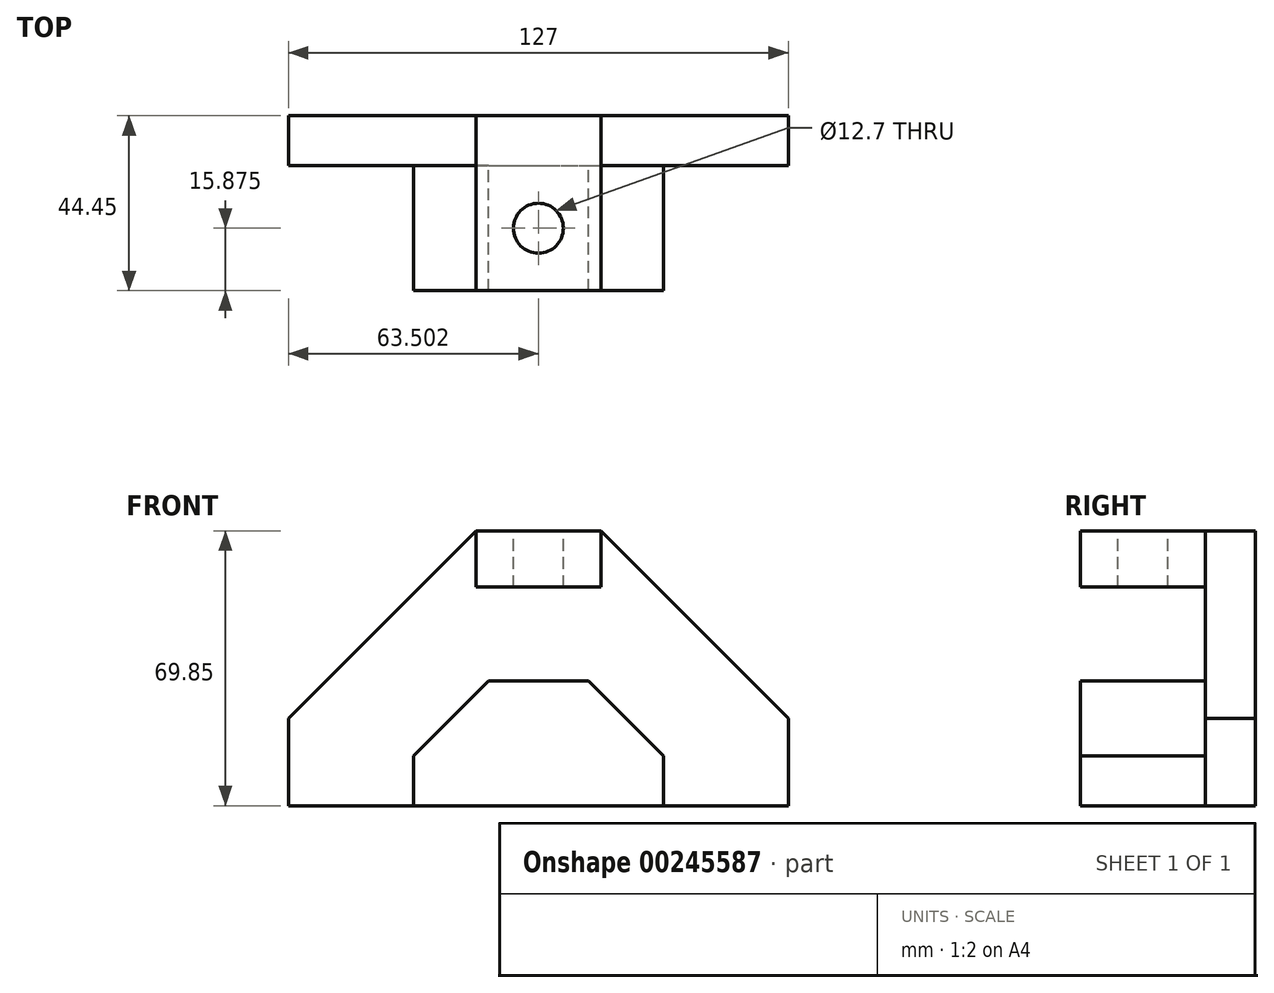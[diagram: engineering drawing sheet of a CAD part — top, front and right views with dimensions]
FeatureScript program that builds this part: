
annotation { "Feature Type Name" : "Feature", "Feature Type Description" : "" }
export const myFeature = defineFeature(function(context is Context, id is Id, definition is map)
    precondition{}
    {
        {
            var Q0;
            Q0=qCreatedBy(makeId("Front.planeOp"),FACE);
            var sketch = newSketch(context, id + "F0", { "sketchPlane" : qUnion([Q0])});
            skLineSegment(sketch, "E0.bottom", {"start": v(-62.96, 52.97) * mm, "end": v(64.04, 52.97) * mm});
            skLineSegment(sketch, "E0.top", {"start": v(-62.96, -16.88) * mm, "end": v(64.04, -16.88) * mm});
            skLineSegment(sketch, "E0.left", {"start": v(-62.96, 52.97) * mm, "end": v(-62.96, -16.88) * mm});
            skLineSegment(sketch, "E0.right", {"start": v(64.04, 52.97) * mm, "end": v(64.04, -16.88) * mm});
            skLineSegment(sketch, "E1", {"start": v(-15.33, 52.97) * mm, "end": v(-62.96, 5.35) * mm});
            skLineSegment(sketch, "E2", {"start": v(16.42, 52.97) * mm, "end": v(64.04, 5.35) * mm});
            skSolve(sketch);
        }
        {
            var Q0;
            {var subQ1=sQuery(id+"F0.wireOp",EDGE,"E0.top");Q0=makeQuery(id+"F0.imprint","IMPRINT",FACE,{"disambiguationData":[TD([[makeQuery(id+"F0.imprint","IMPRINT",EDGE,{"derivedFrom":subQ1}),1.0]])]});}
            extrude(context, id + "F1", {"entities" : qUnion([Q0]), "depth" : 12.7 * mm});
        }
        {
            var Q0;
            Q0=makeQuery(id+"F1.opExtrude","CAP_FACE",FACE,{"disambiguationData":[OSD([sQuery(id+"F0.wireOp",EDGE,"E0.bottom"),sQuery(id+"F0.wireOp",EDGE,"E0.top"),sQuery(id+"F0.wireOp",EDGE,"E0.left"),sQuery(id+"F0.wireOp",EDGE,"E0.right"),sQuery(id+"F0.wireOp",EDGE,"E1"),sQuery(id+"F0.wireOp",EDGE,"E2")])],"isStart":false});
            var sketch = newSketch(context, id + "F2", { "sketchPlane" : qUnion([Q0])});
            skLineSegment(sketch, "E3.right", {"start": v(13.24, 14.87) * mm, "end": v(13.24, -16.88) * mm});
            skLineSegment(sketch, "E4.bottom", {"start": v(13.24, 14.87) * mm, "end": v(32.3, 14.87) * mm});
            skLineSegment(sketch, "E4.top", {"start": v(13.24, -16.88) * mm, "end": v(32.3, -16.88) * mm});
            skLineSegment(sketch, "E4.right", {"start": v(32.3, 14.87) * mm, "end": v(32.3, -16.88) * mm});
            skLineSegment(sketch, "E5", {"start": v(13.24, 14.87) * mm, "end": v(32.3, -4.18) * mm});
            skSolve(sketch);
        }
        {
            var Q0;
            Q0=makeQuery(id+"F1.opExtrude","CAP_FACE",FACE,{"disambiguationData":[OSD([sQuery(id+"F0.wireOp",EDGE,"E0.bottom"),sQuery(id+"F0.wireOp",EDGE,"E0.top"),sQuery(id+"F0.wireOp",EDGE,"E0.left"),sQuery(id+"F0.wireOp",EDGE,"E0.right"),sQuery(id+"F0.wireOp",EDGE,"E1"),sQuery(id+"F0.wireOp",EDGE,"E2")])],"isStart":false});
            var sketch = newSketch(context, id + "F3", { "sketchPlane" : qUnion([Q0])});
            skLineSegment(sketch, "E6.bottom", {"start": v(-12.16, 14.87) * mm, "end": v(13.24, 14.87) * mm});
            skLineSegment(sketch, "E6.top", {"start": v(-12.16, -16.88) * mm, "end": v(13.24, -16.88) * mm});
            skLineSegment(sketch, "E6.left", {"start": v(-12.16, 14.87) * mm, "end": v(-12.16, -16.88) * mm});
            skLineSegment(sketch, "E6.right", {"start": v(13.24, 14.87) * mm, "end": v(13.24, -16.88) * mm});
            skSolve(sketch);
        }
        {
            var Q0;
            Q0=makeQuery(id+"F3.imprint","IMPRINT",FACE,{"disambiguationData":[TD([[makeQuery(id+"F3.imprint","IMPRINT",EDGE,{"derivedFrom":sQuery(id+"F3.wireOp",EDGE,"E6.bottom")}),1.0]])]});
            var sketch = newSketch(context, id + "F4", { "sketchPlane" : qUnion([Q0])});
            skLineSegment(sketch, "E7.bottom", {"start": v(-31.2, -16.88) * mm, "end": v(-12.16, -16.88) * mm});
            skLineSegment(sketch, "E7.top", {"start": v(-31.2, 14.87) * mm, "end": v(-12.16, 14.87) * mm});
            skLineSegment(sketch, "E7.left", {"start": v(-31.2, -16.88) * mm, "end": v(-31.2, 14.87) * mm});
            skLineSegment(sketch, "E7.right", {"start": v(-12.16, -16.88) * mm, "end": v(-12.16, 14.87) * mm});
            skLineSegment(sketch, "E8", {"start": v(-12.16, 14.87) * mm, "end": v(-31.2, -4.18) * mm});
            skSolve(sketch);
        }
        {
            var Q0;
            {var subQ0=sQuery(id+"F4.wireOp",EDGE,"E7.bottom");Q0=makeQuery(id+"F4.imprint","IMPRINT",FACE,{"disambiguationData":[TD([[makeQuery(id+"F4.imprint","IMPRINT",EDGE,{"derivedFrom":subQ0}),1.0]])]});}
            var Q1;
            {var subQ0=sQuery(id+"F2.wireOp",EDGE,"E4.top");Q1=makeQuery(id+"F2.imprint","IMPRINT",FACE,{"disambiguationData":[TD([[makeQuery(id+"F2.imprint","IMPRINT",EDGE,{"derivedFrom":subQ0}),1.0]])]});}
            var Q2;
            Q2=makeQuery(id+"F3.imprint","IMPRINT",FACE,{"disambiguationData":[TD([[makeQuery(id+"F3.imprint","IMPRINT",EDGE,{"derivedFrom":sQuery(id+"F3.wireOp",EDGE,"E6.bottom")}),-1.0]])]});
            extrude(context, id + "F5", {"entities" : qUnion([Q0, Q1, Q2]), "operationType" : NewBodyOperationType.ADD, "depth" : 31.75 * mm});
        }
        {
            var Q0;
            Q0=makeQuery(id+"F1.opExtrude","CAP_FACE",FACE,{"disambiguationData":[OSD([sQuery(id+"F0.wireOp",EDGE,"E0.bottom"),sQuery(id+"F0.wireOp",EDGE,"E0.top"),sQuery(id+"F0.wireOp",EDGE,"E0.left"),sQuery(id+"F0.wireOp",EDGE,"E0.right"),sQuery(id+"F0.wireOp",EDGE,"E1"),sQuery(id+"F0.wireOp",EDGE,"E2")])],"isStart":false});
            var sketch = newSketch(context, id + "F6", { "sketchPlane" : qUnion([Q0])});
            skLineSegment(sketch, "E9.bottom", {"start": v(-15.33, 52.97) * mm, "end": v(16.42, 52.97) * mm});
            skLineSegment(sketch, "E9.top", {"start": v(-15.33, 38.69) * mm, "end": v(16.42, 38.69) * mm});
            skLineSegment(sketch, "E9.left", {"start": v(-15.33, 52.97) * mm, "end": v(-15.33, 38.69) * mm});
            skLineSegment(sketch, "E9.right", {"start": v(16.42, 52.97) * mm, "end": v(16.42, 38.69) * mm});
            skSolve(sketch);
        }
        {
            var Q0;
            Q0=makeQuery(id+"F6.imprint","IMPRINT",FACE,{"disambiguationData":[TD([[makeQuery(id+"F6.imprint","IMPRINT",EDGE,{"derivedFrom":sQuery(id+"F6.wireOp",EDGE,"E9.bottom")}),-1.0]])]});
            var Q1;
            Q1 = qSketchRegion(id + "F8", true);
            extrude(context, id + "F7", {"entities" : qUnion([Q0, Q1]), "operationType" : NewBodyOperationType.ADD, "depth" : 31.75 * mm});
        }
        {
            var Q0;
            Q0=makeQuery(id+"F7.boolean.opBoolean","MERGE",FACE,{"derivedFrom":[makeQuery(id+"F1.opExtrude","SWEPT_FACE",FACE,{"disambiguationData":[OSD([sQuery(id+"F0.wireOp",EDGE,"E0.bottom")])]}),makeQuery(id+"F7.opExtrude","SWEPT_FACE",FACE,{"disambiguationData":[OSD([sQuery(id+"F6.wireOp",EDGE,"E9.bottom")])]})]});
            var sketch = newSketch(context, id + "F8", { "sketchPlane" : qUnion([Q0])});
            skCircle(sketch, "E10", {"center": v(0.54, -28.58) * mm, "radius": 6.35 * mm});
            skSolve(sketch);
        }
        {
            var Q0;
            Q0=makeQuery(id+"F8.imprint","IMPRINT",FACE,{"disambiguationData":[TD([[makeQuery(id+"F8.imprint","IMPRINT",EDGE,{"derivedFrom":sQuery(id+"F8.wireOp",EDGE,"E10")}),1.0]])]});
            extrude(context, id + "F9", {"entities" : qUnion([Q0]), "operationType" : NewBodyOperationType.REMOVE, "oppositeDirection" : true, "depth" : 14.3 * mm});
        }
    });
